# Revit family: FHM_RFA
name_source: partatom
category: Pipe Accessories
units: mm (PartAtom-declared; Revit-internal decimal feet)

## family parameters
Always vertical = Yes
Cut with Voids When Loaded = No
OmniClass Number = 23.65.55.14.17
OmniClass Title = Adjusting/Controlling Valves for Liquid Services
Part Type = Normal
Round Connector Dimension = Use Diameter
Shared = No
Work Plane-Based = No

## types (2) — shared parameters
Description = Supply Temperature Control
IfcExportAs = IfcValveType
IfcExportType = FHM
L = 176 mm
LOD 200 = No
LOD 350 = Yes
Manufacturer = Danfoss
Max Differential Pressure = 0.6 bar
Max Operating Pressure = 10 bar
Max Working Temperature = 90 °C
Power Supply = 230 V AC
URL = https://store.danfoss.com
Valve Body Material = Danfoss Brass
W = 40 mm  [stored 0.131234 ft]

## per-type parameters (varying)
| type | FTC | H | Model | Model Type | Setting Temperature Range | Weight |
| FHM_C2_088U0092 | No | 312 mm  [stored 1.02362 ft] | 088U0092 | FHM_C2_Mixing shunt |  | 3.83 kg |
| FHM_C1_088U0094 | Yes | 384 mm | 088U0094 | FHM_C1_Mixing shunt | 18-50°C | 4.06 kg |

note: [stored X ft] marks values corroborated as IEEE doubles in the binary element streams (Revit-internal decimal feet)

## geometry (parser evidence)
native form markers: Blend x2, Sweep x11
no freeform markers — native parametric forms only
